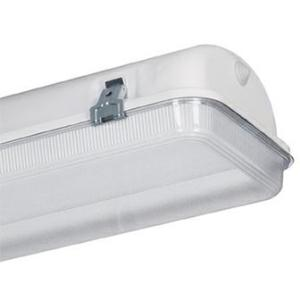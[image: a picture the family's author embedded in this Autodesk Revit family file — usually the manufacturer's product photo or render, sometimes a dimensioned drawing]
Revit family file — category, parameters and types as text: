
# Revit family: 3f_filippi_-_beta_i3f_75_pc_ampio_3f_filippi_-_55611_-_i3f_led_752x30w_ep_ampio_l1565
name_source: partatom
category: Lighting Fixtures
units: mm (PartAtom-declared; Revit-internal decimal feet)

## family parameters
Cut with Voids When Loaded = No
Host = Face
Light Source = No
Part Type = Normal
Room Calculation Point = No
Round Connector Dimension = Use Diameter
Shared = No

## types (1)
- 3F Filippi - Beta i3F 75 PC Ampio (1 x LED, 9715 lm, 67 W, 4000 K)
    Apparent Load = 67 VA
    Approval mark = ENEC
    CIE Flux Codes = 52 82 96 97 100
    Color Rendering = 80
    Color Temperature = 4000 K
    Control Gear = Electronic ballast
    Default Elevation = 1800 mm
    Description = ILLUMINOTECHNICAL
Luminous efficiency 100% (DLOR 97%, ULOR 3%).
Initial luminous flux of the luminaire 9715 lm.
Emergency luminaire luminous flux BLF 5.7%.
Wide symmetric distribution.
Installation Interdistance Transv.D = 1.27 x hu - Long.D = 1.26 x hu.
Tabular UGR (CIE 117 - 4H-8H; S=0.25H; 70/50/20): RUG 20.6 - 22.4.
Beam angle: 92° - 100°.
Luminous efficacy 145 lm/W.
Lifetime (L93/B10): 30000 h. (tq+25°C)
Lifetime (L90/B10): 50000 h. (tq+25°C)
Lifetime (L85/B10): 80000 h. (tq+25°C)
Lifetime (L80/B10): 100000 h. (tq+25°C)
Sudden decreased luminous flux after 50000 hours: 0% (C0).
Photobiological safety in compliance with IEC/TR 62778: RG0 risk exempt, (IEC 62471).
In compliance with IEC/EN 62722-2-1 - IEC/EN 62717 standards.

SOURCE
2 linear LED modules 30W/840.
Energy efficiency class (UE 2019/2020 - UE 2019/2015): D.
CIE 13.3 Colour rendering index: CRI >80 (R9 <50%).
IES TM-30 Fidelity Index: Rf = 84 Rg = 95.
CCT nominal colour temperature 4000 K.
Colour initial tolerance (MacAdam): SDCM 3.

MECHANICAL
Single-piece housing in pressed steel, powder-coated in white epoxy-polyester.
Diffuser in self-extinguishing V2 polycarbonate, photo-engraved interior, UV stabilised, injection moulded, with smooth outer surface, sealing gasket, hinged opening by means of galvanised steel clips.
Wide flow recuperator, oversized, in specular aluminium with superficial titanium-magnesium treatment, non-iridescent.
Gear-tray unit in hot-galvanised steel, painted in white polyester, fixed to the housing by means of "Ribloc" rapid devices in galvanised steel, hinged opening.
Luminaire with limited surface temperature. - D - (EN 60598-2-24)
Dimensions: 1565x235 mm, height 135 mm. Weight 7.3 kg.
IP65 protection degree.
Mechanical strength to impacts IK10 (20 joule).
Glow-wire test resistance 850°C.

ELECTRICAL
Halogen Free electronic wiring 230V-50/60Hz, power factor 0.95, THD <25%, constant output current, SELV, class I, 1 driver.
Power of the luminaire 67 W.
CE - IEC 60598-1 - EN 60598-1.
EP maintained emergency wiring on board, 1h duration, 24h recharge; compliant with EN 60598-2-22, excluding high risk areas.
SAFE FLICKER: PstLM=<1 and SVM=<0.4 (IEC TR 61547-1 and IEC TR 63158), to ensure a more comfortable and safe light.
Ambient temperature from +5°C to +25°C.
Temperature class T6 max 85°C.
Relative humidity UR: <85%.

INSTALLATION
Ceiling / Suspended / Wall.
All accessories dedicated to this product are available on the Catalog and on our website www.3F-Filippi.com.

APPLICATIONS
Suitable product for food production plants (HACCP), IFS (Food Version 6), BRC (GSFS Food Version 7).
In industrial environments, stores and dry, dusty indoor environments, subject to occasional water splashes.

WARNING
Fixture not suitable for cold stores with an ambient temperature <5°C and/or relative humidity >85%.
Luminaire designed for disposal/recycling at end-of-life.
Replaceable (LED only) light source by a professional. Replaceable control gear by a professional.
    Height = 135 mm
    Lamp = 1 x LED
    Lamp Light Flux = 9715 lm
    Lamp Power = 67 W
    Lamp count = 1
    Length = 1565 mm
    Lifetime = 50000 h
    Luminous efficacy = 145 lm/W
    Manufacturer = 3F Filippi
    ModVariant = No
    Model = 3F Filippi - 55611 - i3F LED 752x30W EP AMPIO L1565
    Mounting Place = Ceiling
    Mounting Type = Pendant
    Number of Poles = 1
    OnlyDefault = Yes
    Power Factor = 1
    Product Name = 3F Filippi - Beta i3F 75 PC Ampio
    Product group = pendant luminaire
    ProductGroupID = 9
    Protection Class = Protection class I
    Protection Degree = IP 65
    RLX_Detail_Level = 1
    RLX_Emergency_Light_Flux = 0 lm
    RLX_Emergency_Type = 0
    RLX_Emergency_Type_DB = No
    RlxData = <blob elided: 67837 chars, md5=a143aa3d>
    Socket = socket
    Standby Power = 0 W
    System Light Flux = 9715 lm
    System Power = 67 W
    Type Comments = Product without accessories
    Type Image = 3ffilippi_55611.jpg
    URL = http://relux.com
    VarID = ---
    Voltage = 0 V
    Weight = 0.00 kg
    Width = 235 mm

## geometry (parser evidence)
native form markers: Blend x4, Sweep x8
no freeform markers — native parametric forms only
